AUTODESK INVENTOR PART (.ipt)
format: ipt  version: 2017 (Build 210142000, 142)  size: 201,728 bytes
history: native  units: mm
features: other x9, sketch x6, extrude x5, plane x3, pattern_circular x2, fillet x1, mirror x1, revolve x1
ambient origin geometry x8: Origin, YZ Plane, XZ Plane, XY Plane, X Axis, Y Axis, Z Axis, Center Point
bodies: Solid2 (feature_tree)
feature tree (28):
  other  "Table"
  other  "Part Number = Rotameter 165 DE16"
  other  "Part Number = Rotameter 170 DE20"
  other  "Part Number = Rotameter 185 DE25"
  other  "Part Number = Rotameter 200 DE32"
  other  "Part Number = Rotameter 350 DE40"
  other  "Part Number = Rotameter 350 DE50"
  other  "Part Number = Rotameter 350 DE63"
  other  "Part Number = Rotameter 350 DE75"
  extrude  "Extrusion2"  Depth=11.0998mm
  extrude  "Extrusion1"  Depth=20.0mm TaperAngle=180.0deg
  pattern_circular  "Circular Pattern1"  [2 undecoded]
  extrude  "Extrusion7"  Depth=1.0mm TaperAngle=0.0deg
  fillet  "Fillet1"  Radius=3.721369mm
  plane  "Work Plane2"
  extrude  "Extrusion8"  Depth=85.0mm
  sketch  "Sketch11"  dims[d22=9.0932mm]
  plane  "Work Plane3"
  extrude  "Extrusion9"  TaperAngle=360.0deg  [1 undecoded]
  pattern_circular  "Circular Pattern2"  [2 undecoded]
  plane  "Work Plane4"
  mirror  "Mirror2"
  revolve  "Revolution2"  [1 undecoded]
  sketch  "Sketch1"  dims[d6=0.0mm d7=11.0998mm]
  sketch  "Sketch9"  dims[d8=0.0mm d9=20.0mm d10=180.0deg]
  sketch  "Sketch10"  dims[d21=27.2796mm]
  sketch  "Sketch12"  dims[d23=0.0mm d24=0.0mm]
  sketch  "Sketch13"  dims[d27=3.0mm d28=11.0998mm d29=1.0mm d30=0.0mm d31=3.721369mm d32=85.0mm d33=360.0deg d35=15.22976mm d36=0.5mm d37=0.0mm d38=152.2976mm d40=11.0998mm d41=100.0mm d42=40.0mm d43=90.0deg d44=0.0mm d45=0.0mm]
note: 6 required parameter values undecoded (feature->parameter linkage not recoverable at this tier; creation-order binding heuristic only, values carry confidence <= 0.55)